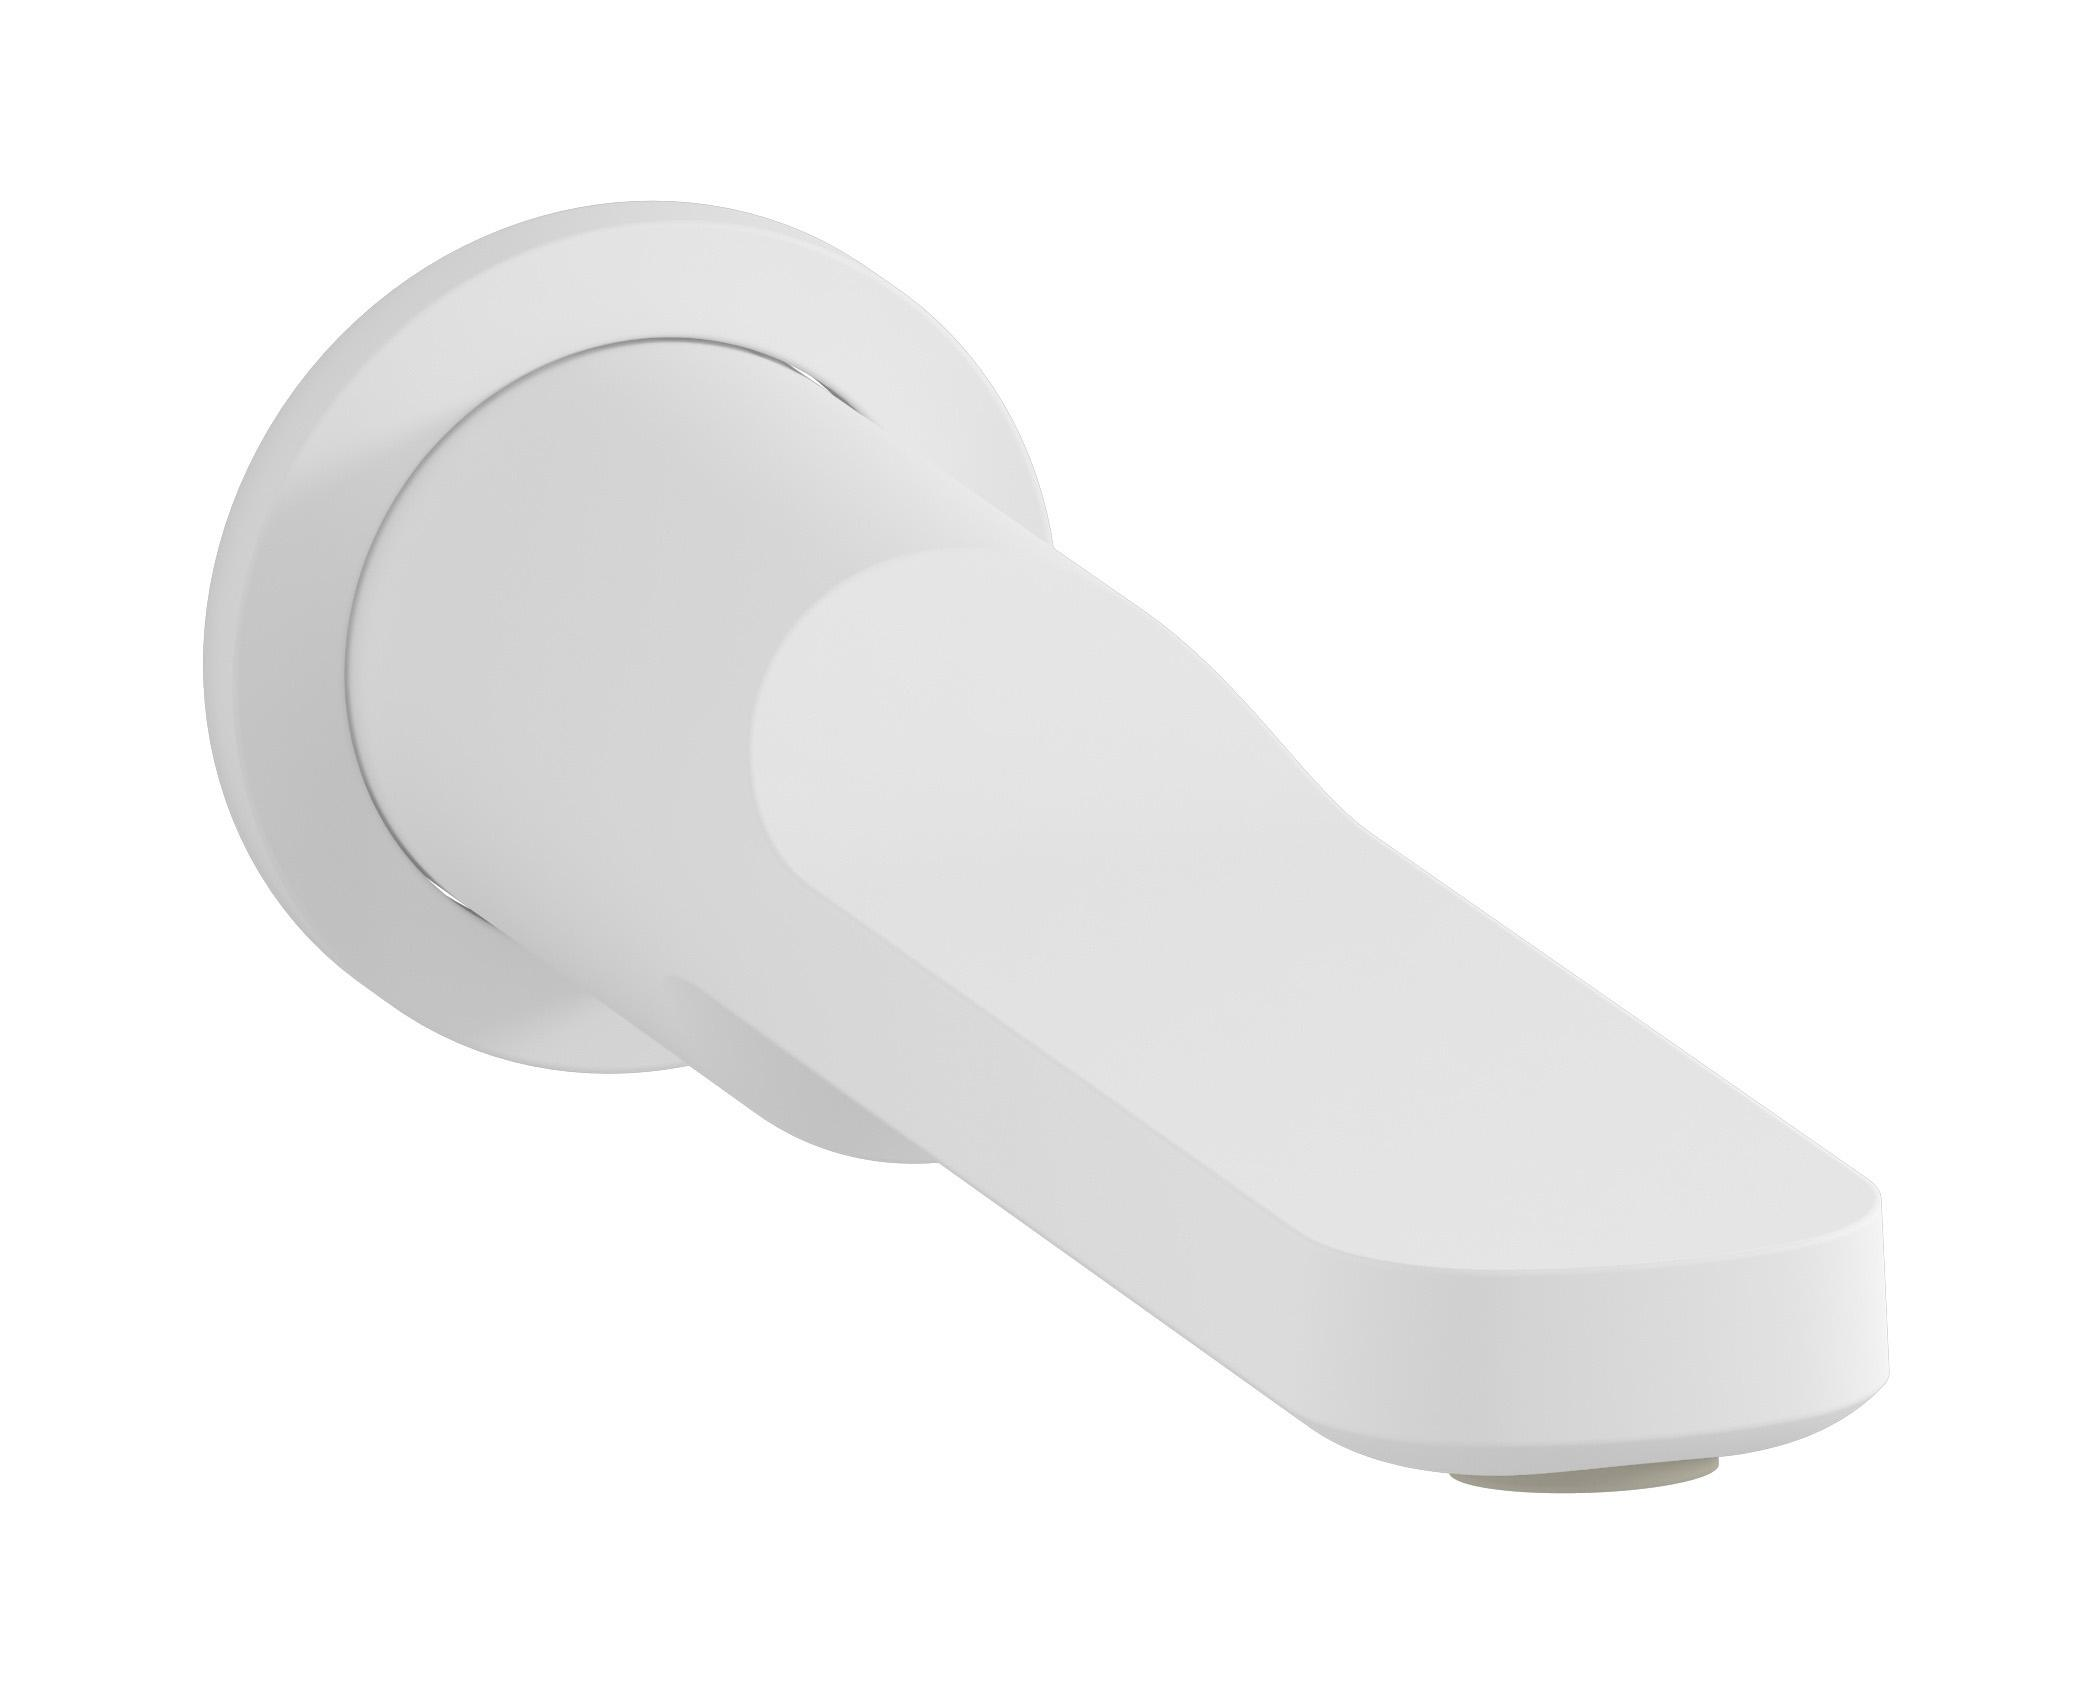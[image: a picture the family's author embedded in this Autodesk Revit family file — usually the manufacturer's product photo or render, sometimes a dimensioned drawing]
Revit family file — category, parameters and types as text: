
# Revit family: AA320
name_source: partatom
category: Apparecchi idraulici
units: mm (PartAtom-declared; Revit-internal decimal feet)

## family parameters
Basato su piano di lavoro = No
Condiviso = No
Mantieni orientamento annotazione = No
Numero OmniClass = 23.45.55.17
Punto di calcolo locali = No
Quota connettore circolare = Usa diametro
Sempre verticale = Sì
Taglio con vuoti quando caricato = No
Tipo di parte = Normale
Titolo OmniClass = Mixing Faucets

## types (5) — shared parameters
Commenti sul tipo = Spout
Connessione CW = No
Connessione HW = No
Connessione di scarico = No
Connessione di ventilazione = No
Descrizione = Wall mounted spout
Produttore = IB Rubinetterie S.p.A.
URL = https://www.weareib.it
Water inlet = 10 mm  [stored 0.0328084 ft]
zero-valued in all types: Prospetto di default

## per-type parameters (varying)
| type | Finishes surface | Immagine tipo | Modello |
| Chrome | IB_Chrome | AA320CC.jpg | AA320CC |
| Brushed nickel | IB_Brushed nickel | AA320SS.jpg | AA320SS |
| Matt black | IB_matt black | AA320NP.jpg | AA320NP |
| Matt white | IB_matt white | AA320BO.jpg | AA320BO |
| Brushed gold | IB_brushed gold | AA320OS.jpg | AA320OS |

note: [stored X ft] marks values corroborated as IEEE doubles in the binary element streams (Revit-internal decimal feet)
